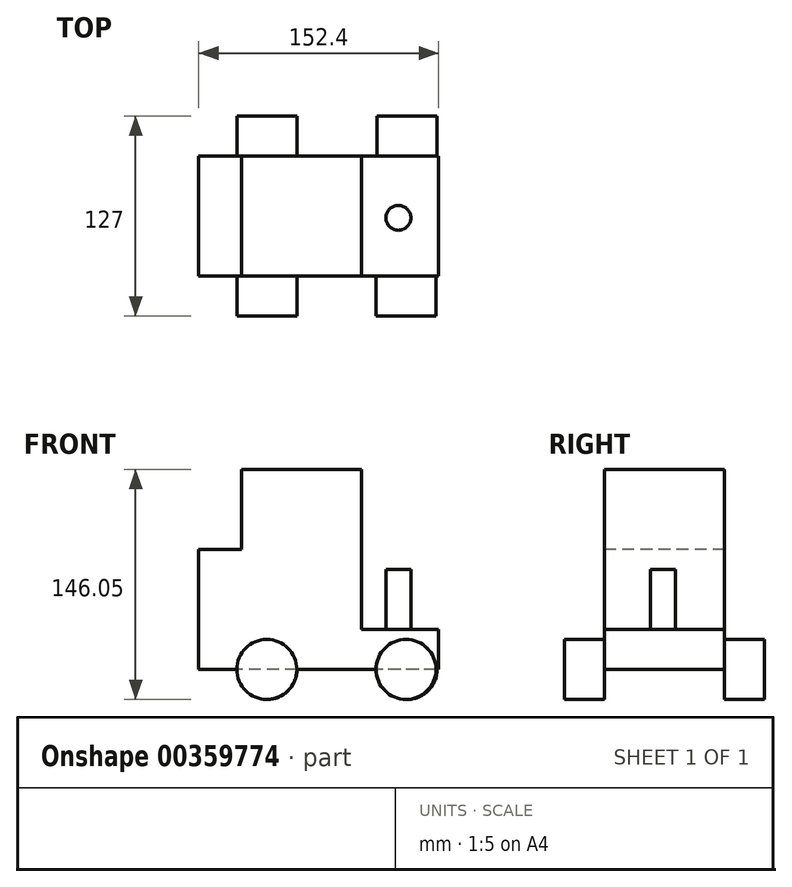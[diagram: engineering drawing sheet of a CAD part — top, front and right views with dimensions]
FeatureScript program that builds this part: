
annotation { "Feature Type Name" : "Feature", "Feature Type Description" : "" }
export const myFeature = defineFeature(function(context is Context, id is Id, definition is map)
    precondition{}
    {
        {
            var Q0;
            Q0=qCreatedBy(makeId("Front.planeOp"),FACE);
            var sketch = newSketch(context, id + "F0", { "sketchPlane" : qUnion([Q0])});
            skLineSegment(sketch, "E0.bottom", {"start": v(76.2, 63.5) * mm, "end": v(-76.2, 63.5) * mm});
            skLineSegment(sketch, "E0.top", {"start": v(76.2, -63.5) * mm, "end": v(-76.2, -63.5) * mm});
            skLineSegment(sketch, "E0.left", {"start": v(76.2, 63.5) * mm, "end": v(76.2, -63.5) * mm});
            skLineSegment(sketch, "E0.right", {"start": v(-76.2, 63.5) * mm, "end": v(-76.2, -63.5) * mm});
            skPoint(sketch, "E0.middle", {"position": v(0, 0) * mm});
            skSolve(sketch);
        }
        {
            var Q0;
            Q0 = qSketchRegion(id + "F0", true);
            extrude(context, id + "F1", {"entities" : qUnion([Q0]), "depth" : 76.2 * mm});
        }
        {
            var Q0;
            Q0=makeQuery(id+"F1.opExtrude","CAP_FACE",FACE,{"disambiguationData":[OSD([sQuery(id+"F0.wireOp",EDGE,"E0.bottom"),sQuery(id+"F0.wireOp",EDGE,"E0.top"),sQuery(id+"F0.wireOp",EDGE,"E0.left"),sQuery(id+"F0.wireOp",EDGE,"E0.right")])],"isStart":false});
            var sketch = newSketch(context, id + "F2", { "sketchPlane" : qUnion([Q0])});
            skLineSegment(sketch, "E1", {"start": v(-76.2, 12.7) * mm, "end": v(-49.08, 12.7) * mm});
            skLineSegment(sketch, "E2", {"start": v(-49.08, 12.7) * mm, "end": v(-49.08, 63.5) * mm});
            skLineSegment(sketch, "E3", {"start": v(-49.08, 63.5) * mm, "end": v(27.12, 63.5) * mm});
            skLineSegment(sketch, "E4", {"start": v(76.2, -63.5) * mm, "end": v(76.2, -38.1) * mm});
            skLineSegment(sketch, "E5", {"start": v(27.12, 63.5) * mm, "end": v(27.12, -38.1) * mm});
            skLineSegment(sketch, "E6", {"start": v(27.12, -38.1) * mm, "end": v(76.2, -38.1) * mm});
            skLineSegment(sketch, "E7", {"start": v(42.24, -38.1) * mm, "end": v(42.24, 0) * mm});
            skLineSegment(sketch, "E8", {"start": v(58.36, 0) * mm, "end": v(58.36, -38.1) * mm});
            skLineSegment(sketch, "E9", {"start": v(42.24, 0) * mm, "end": v(58.36, 0) * mm});
            skSolve(sketch);
        }
        {
            var Q0;
            {var subQ0=sQuery(id+"F2.wireOp",EDGE,"E1");Q0=makeQuery(id+"F2.imprint","IMPRINT",FACE,{"disambiguationData":[TD([[makeQuery(id+"F2.imprint","IMPRINT",EDGE,{"derivedFrom":subQ0}),1.0]])]});}
            var Q1;
            {var subQ5=sQuery(id+"F2.wireOp",EDGE,"E5");Q1=makeQuery(id+"F2.imprint","IMPRINT",FACE,{"disambiguationData":[TD([[makeQuery(id+"F2.imprint","IMPRINT",EDGE,{"derivedFrom":subQ5}),1.0]])]});}
            extrude(context, id + "F3", {"entities" : qUnion([Q0, Q1]), "operationType" : NewBodyOperationType.REMOVE, "endBound" : BoundingType.THROUGH_ALL, "oppositeDirection" : true, "depth" : 25.4 * mm});
        }
        {
            var Q0;
            Q0=makeQuery(id+"F1.opExtrude","CAP_FACE",FACE,{"disambiguationData":[OSD([sQuery(id+"F0.wireOp",EDGE,"E0.bottom"),sQuery(id+"F0.wireOp",EDGE,"E0.top"),sQuery(id+"F0.wireOp",EDGE,"E0.left"),sQuery(id+"F0.wireOp",EDGE,"E0.right")])],"isStart":false});
            var sketch = newSketch(context, id + "F4", { "sketchPlane" : qUnion([Q0])});
            skCircle(sketch, "E10", {"center": v(-32.98, -63.5) * mm, "radius": 19.05 * mm});
            skCircle(sketch, "E11", {"center": v(55.41, -63.5) * mm, "radius": 19.05 * mm});
            skSolve(sketch);
        }
        {
            var Q0;
            Q0 = qSketchRegion(id + "F4", true);
            extrude(context, id + "F5", {"entities" : qUnion([Q0]), "operationType" : NewBodyOperationType.ADD, "depth" : 25.4 * mm});
        }
        {
            var Q0;
            Q0=makeQuery(id+"F1.opExtrude","CAP_FACE",FACE,{"disambiguationData":[OSD([sQuery(id+"F0.wireOp",EDGE,"E0.bottom"),sQuery(id+"F0.wireOp",EDGE,"E0.top"),sQuery(id+"F0.wireOp",EDGE,"E0.left"),sQuery(id+"F0.wireOp",EDGE,"E0.right")])],"isStart":true});
            var sketch = newSketch(context, id + "F6", { "sketchPlane" : qUnion([Q0])});
            skCircle(sketch, "E12", {"center": v(-56.1, -63.5) * mm, "radius": 19.05 * mm});
            skCircle(sketch, "E13", {"center": v(32.89, -63.5) * mm, "radius": 19.05 * mm});
            skSolve(sketch);
        }
        {
            var Q0;
            {var subQ0=sQuery(id+"F6.wireOp",EDGE,"E13");var subQ1=makeQuery(id+"F1.opExtrude","CAP_EDGE",EDGE,{"disambiguationData":[OSD([sQuery(id+"F0.wireOp",EDGE,"E0.top")])],"isStart":true});var subQ2=makeQuery(id+"F6.imprint","INTERSECT",VERTEX,{"disambiguationData":[OD(0.0)],"derivedFrom":[subQ1,subQ0]});Q0=makeQuery(id+"F6.imprint","IMPRINT",FACE,{"disambiguationData":[TD([[makeQuery(id+"F6.imprint","IMPRINT",EDGE,{"disambiguationData":[TD([[subQ2,1.0]])],"derivedFrom":subQ0}),1.0]])]});}
            var Q1;
            {var subQ0=sQuery(id+"F6.wireOp",EDGE,"E12");var subQ1=makeQuery(id+"F1.opExtrude","CAP_EDGE",EDGE,{"disambiguationData":[OSD([sQuery(id+"F0.wireOp",EDGE,"E0.top")])],"isStart":true});var subQ2=makeQuery(id+"F6.imprint","INTERSECT",VERTEX,{"disambiguationData":[OD(0.0)],"derivedFrom":[subQ1,subQ0]});Q1=makeQuery(id+"F6.imprint","IMPRINT",FACE,{"disambiguationData":[TD([[makeQuery(id+"F6.imprint","IMPRINT",EDGE,{"disambiguationData":[TD([[subQ2,1.0]])],"derivedFrom":subQ0}),1.0]])]});}
            var Q2;
            {var subQ0=sQuery(id+"F6.wireOp",EDGE,"E13");var subQ1=makeQuery(id+"F1.opExtrude","CAP_EDGE",EDGE,{"disambiguationData":[OSD([sQuery(id+"F0.wireOp",EDGE,"E0.top")])],"isStart":true});var subQ2=makeQuery(id+"F6.imprint","INTERSECT",VERTEX,{"disambiguationData":[OD(0.0)],"derivedFrom":[subQ1,subQ0]});Q2=makeQuery(id+"F6.imprint","IMPRINT",FACE,{"disambiguationData":[TD([[makeQuery(id+"F6.imprint","IMPRINT",EDGE,{"disambiguationData":[TD([[subQ2,-1.0]])],"derivedFrom":subQ0}),1.0]])]});}
            var Q3;
            {var subQ0=sQuery(id+"F6.wireOp",EDGE,"E12");var subQ1=makeQuery(id+"F1.opExtrude","CAP_EDGE",EDGE,{"disambiguationData":[OSD([sQuery(id+"F0.wireOp",EDGE,"E0.top")])],"isStart":true});var subQ2=makeQuery(id+"F6.imprint","INTERSECT",VERTEX,{"disambiguationData":[OD(0.0)],"derivedFrom":[subQ1,subQ0]});Q3=makeQuery(id+"F6.imprint","IMPRINT",FACE,{"disambiguationData":[TD([[makeQuery(id+"F6.imprint","IMPRINT",EDGE,{"disambiguationData":[TD([[subQ2,-1.0]])],"derivedFrom":subQ0}),1.0]])]});}
            extrude(context, id + "F7", {"entities" : qUnion([Q0, Q1, Q2, Q3]), "operationType" : NewBodyOperationType.ADD, "depth" : 25.4 * mm});
        }
        {
            var Q0;
            Q0=qCreatedBy(makeId("Top.planeOp"),FACE);
            var sketch = newSketch(context, id + "F8", { "sketchPlane" : qUnion([Q0])});
            skCircle(sketch, "E14", {"center": v(50.55, -39.24) * mm, "radius": 7.93 * mm});
            skSolve(sketch);
        }
        {
            var Q0;
            Q0=makeQuery(id+"F3.boolean.opBoolean","COPY",FACE,{"derivedFrom":makeQuery(id+"F3.opExtrude","SWEPT_FACE",FACE,{"disambiguationData":[OSD([sQuery(id+"F2.wireOp",EDGE,"E9")])]})});
            extrude(context, id + "F9", {"entities" : qUnion([Q0]), "operationType" : NewBodyOperationType.REMOVE, "oppositeDirection" : true, "depth" : 38.1 * mm});
        }
        {
            var Q0;
            Q0=makeQuery(id+"F8.imprint","IMPRINT",FACE,{"disambiguationData":[TD([[makeQuery(id+"F8.imprint","IMPRINT",EDGE,{"derivedFrom":sQuery(id+"F8.wireOp",EDGE,"E14")}),1.0]])]});
            extrude(context, id + "F10", {"entities" : qUnion([Q0]), "operationType" : NewBodyOperationType.ADD, "oppositeDirection" : true, "depth" : 40.64 * mm});
        }
    });
